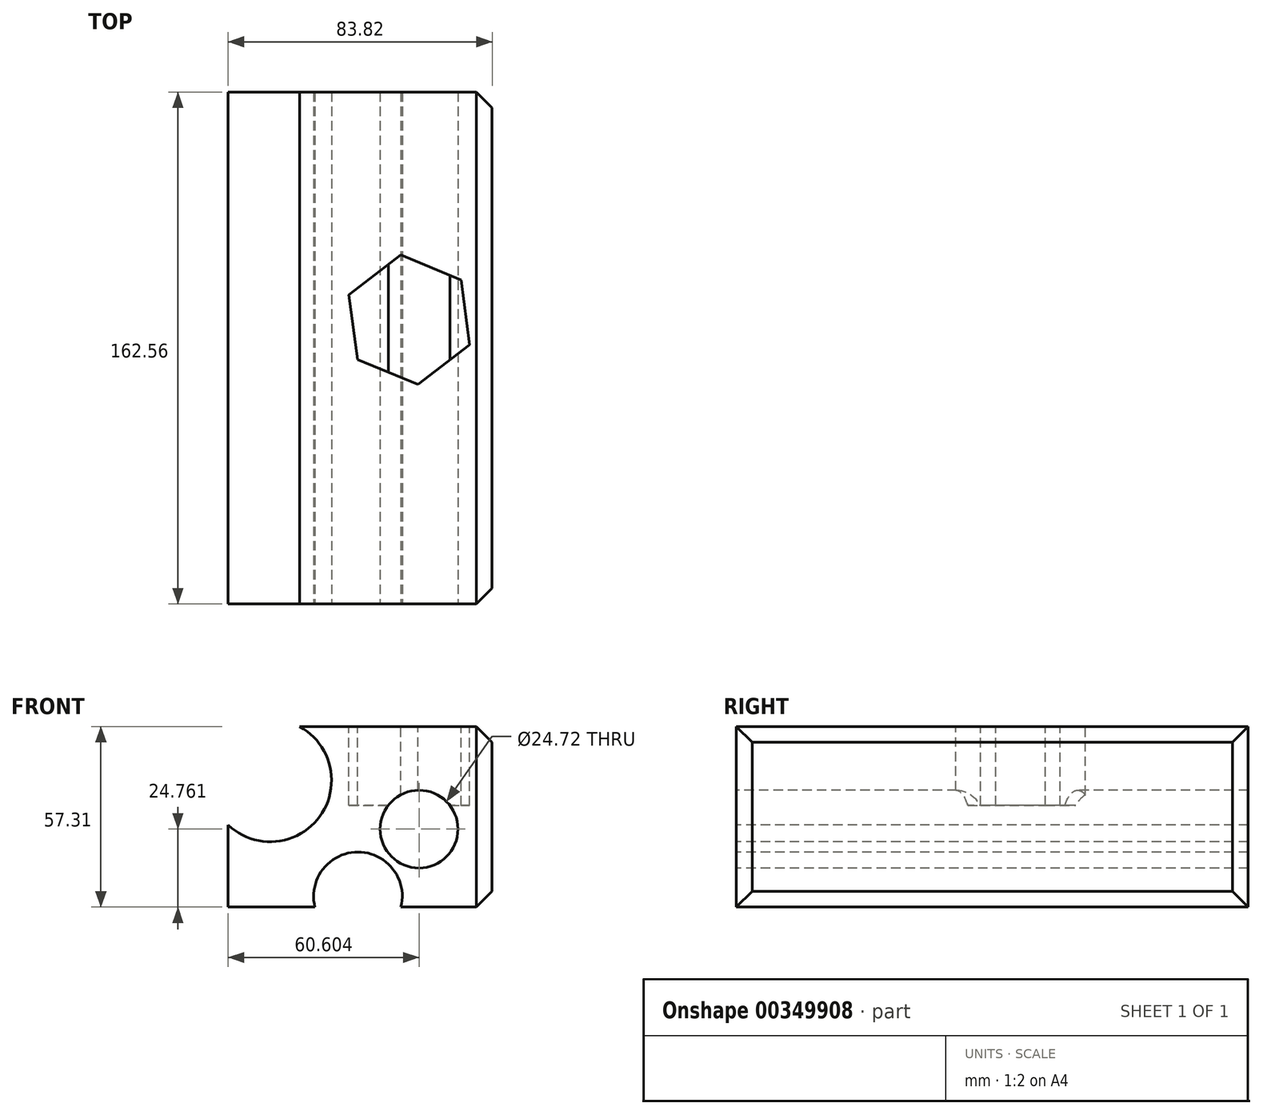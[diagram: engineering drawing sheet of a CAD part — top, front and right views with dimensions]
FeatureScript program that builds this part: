
annotation { "Feature Type Name" : "Feature", "Feature Type Description" : "" }
export const myFeature = defineFeature(function(context is Context, id is Id, definition is map)
    precondition{}
    {
        {
            var Q0;
            Q0=qCreatedBy(makeId("Front.planeOp"),FACE);
            var sketch = newSketch(context, id + "F0", { "sketchPlane" : qUnion([Q0])});
            skLineSegment(sketch, "E0.bottom", {"start": v(-38.43, 17.06) * mm, "end": v(45.39, 17.06) * mm});
            skLineSegment(sketch, "E0.top", {"start": v(-38.43, -40.25) * mm, "end": v(45.39, -40.25) * mm});
            skLineSegment(sketch, "E0.left", {"start": v(-38.43, 17.06) * mm, "end": v(-38.43, -40.25) * mm});
            skLineSegment(sketch, "E0.right", {"start": v(45.39, 17.06) * mm, "end": v(45.39, -40.25) * mm});
            skSolve(sketch);
        }
        {
            var Q0;
            Q0=makeQuery(id+"F0.imprint","IMPRINT",FACE,{"disambiguationData":[TD([[makeQuery(id+"F0.imprint","IMPRINT",EDGE,{"derivedFrom":sQuery(id+"F0.wireOp",EDGE,"E0.bottom")}),-1.0]])]});
            extrude(context, id + "F1", {"entities" : qUnion([Q0]), "depth" : 162.56 * mm});
        }
        {
            var Q0;
            Q0=makeQuery(id+"F1.opExtrude","CAP_FACE",FACE,{"disambiguationData":[OSD([sQuery(id+"F0.wireOp",EDGE,"E0.bottom"),sQuery(id+"F0.wireOp",EDGE,"E0.top"),sQuery(id+"F0.wireOp",EDGE,"E0.left"),sQuery(id+"F0.wireOp",EDGE,"E0.right")])],"isStart":false});
            var sketch = newSketch(context, id + "F2", { "sketchPlane" : qUnion([Q0])});
            skCircle(sketch, "E1", {"center": v(-25.1, 0) * mm, "radius": 19.48 * mm});
            skCircle(sketch, "E2", {"center": v(22.17, -15.49) * mm, "radius": 12.36 * mm});
            skCircle(sketch, "E3", {"center": v(2.77, -36.85) * mm, "radius": 14.08 * mm});
            skSolve(sketch);
        }
        {
            var Q0;
            Q0 = qSketchRegion(id + "F2", true);
            extrude(context, id + "F3", {"entities" : qUnion([Q0]), "operationType" : NewBodyOperationType.REMOVE, "endBound" : BoundingType.THROUGH_ALL, "oppositeDirection" : true, "depth" : 25 * mm});
        }
        {
            var Q0;
            {var subQ0=sQuery(id+"F0.wireOp",EDGE,"E0.right");var subQ3=sQuery(id+"F0.wireOp",EDGE,"E0.bottom");Q0=makeQuery(id+"F3.boolean.opBoolean","SPLIT",FACE,{"disambiguationData":[TD([makeQuery(id+"F1.opExtrude","SWEPT_FACE",FACE,{"disambiguationData":[OSD([subQ0])]})])],"derivedFrom":makeQuery(id+"F1.opExtrude","SWEPT_FACE",FACE,{"disambiguationData":[OSD([subQ3])]})});}
            var sketch = newSketch(context, id + "F4", { "sketchPlane" : qUnion([Q0])});
            skCircle(sketch, "E4.cCircle", {"center": v(19.07, -72.3) * mm, "radius": 17.97 * mm, "construction": true});
            skLineSegment(sketch, "E4.0", {"start": v(38.24, -80.22) * mm, "end": v(21.8, -92.87) * mm});
            skLineSegment(sketch, "E4.1", {"start": v(21.8, -92.87) * mm, "end": v(2.62, -84.96) * mm});
            skLineSegment(sketch, "E4.2", {"start": v(2.62, -84.96) * mm, "end": v(-0.11, -64.39) * mm});
            skLineSegment(sketch, "E4.3", {"start": v(-0.11, -64.39) * mm, "end": v(16.33, -51.74) * mm});
            skLineSegment(sketch, "E4.4", {"start": v(16.33, -51.74) * mm, "end": v(35.51, -59.66) * mm});
            skLineSegment(sketch, "E4.5", {"start": v(35.51, -59.66) * mm, "end": v(38.24, -80.22) * mm});
            skPoint(sketch, "E4.0.midPoint", {"position": v(30.02, -86.55) * mm});
            skSolve(sketch);
        }
        {
            var Q0;
            Q0=makeQuery(id+"F4.imprint","IMPRINT",FACE,{"disambiguationData":[TD([[makeQuery(id+"F4.imprint","IMPRINT",EDGE,{"derivedFrom":sQuery(id+"F4.wireOp",EDGE,"E4.0")}),-1.0]])]});
            extrude(context, id + "F5", {"entities" : qUnion([Q0]), "operationType" : NewBodyOperationType.REMOVE, "oppositeDirection" : true, "depth" : 25 * mm});
        }
        {
            var Q0;
            Q0=makeQuery(id+"F3.boolean.opBoolean","SPLIT",BODY,{"disambiguationData":[OD(0.0)],"derivedFrom":makeQuery(id+"F1.opExtrude","SWEPT_BODY",BODY,{"disambiguationData":[OSD([sQuery(id+"F0.wireOp",EDGE,"E0.bottom"),sQuery(id+"F0.wireOp",EDGE,"E0.top"),sQuery(id+"F0.wireOp",EDGE,"E0.left"),sQuery(id+"F0.wireOp",EDGE,"E0.right")])]})});
            deleteBodies(context, id + "F6", {"entities" : qUnion([Q0])});
        }
        {
            var Q0;
            Q0=makeQuery(id+"F1.opExtrude","SWEPT_FACE",FACE,{"disambiguationData":[OSD([sQuery(id+"F0.wireOp",EDGE,"E0.right")])]});
            chamfer(context, id + "F7", {"entities" : qUnion([Q0]), "width" : 5 * mm, "tangentPropagation" : true});
        }
    });
